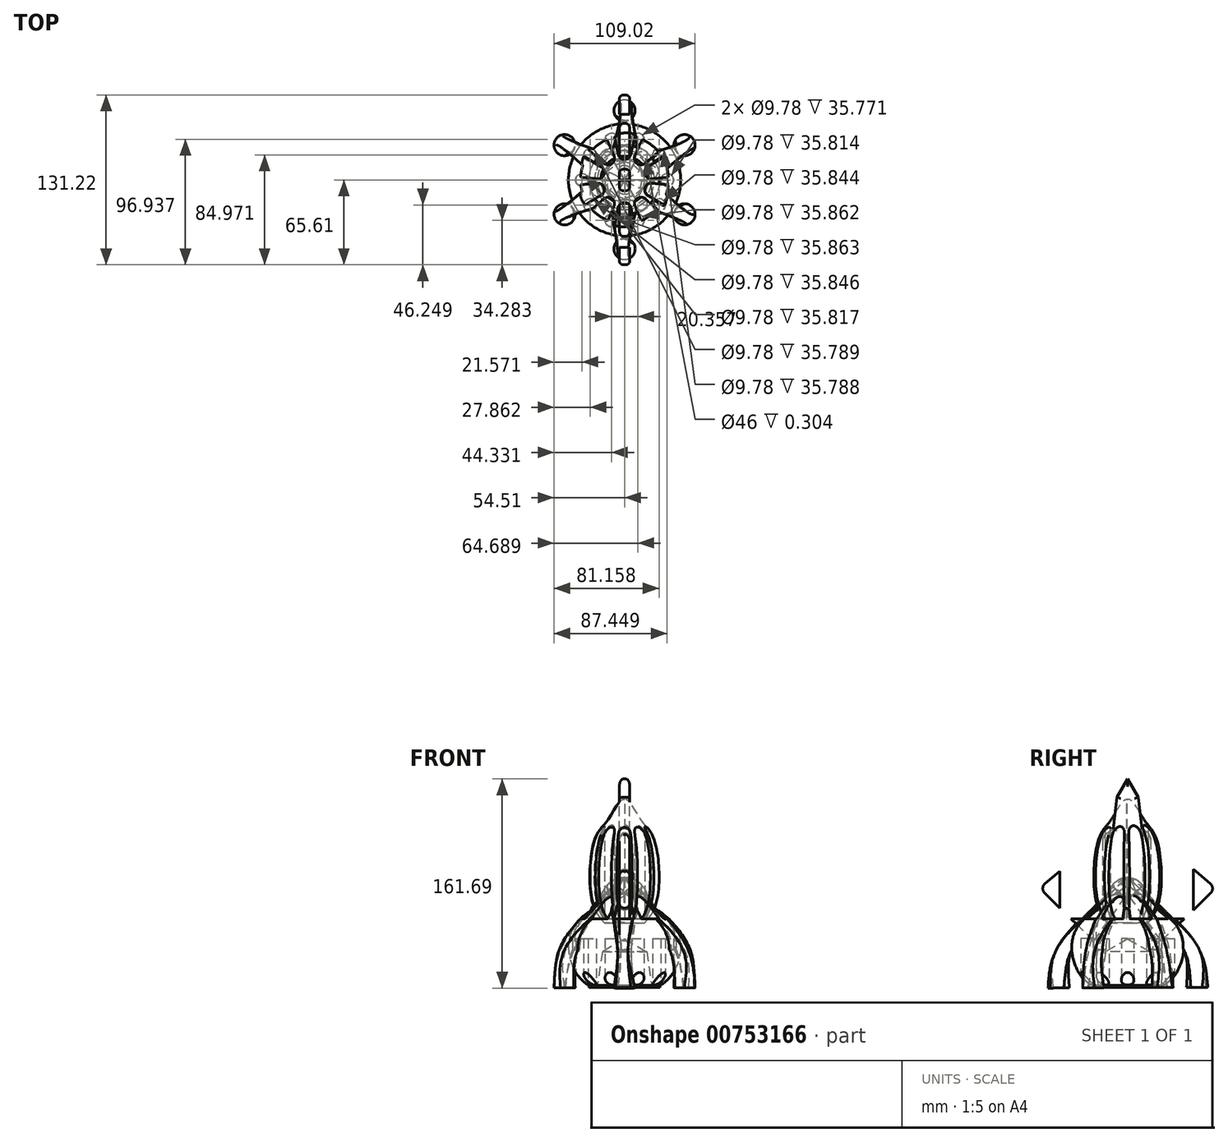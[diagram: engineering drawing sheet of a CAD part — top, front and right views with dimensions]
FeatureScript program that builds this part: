
annotation { "Feature Type Name" : "Feature", "Feature Type Description" : "" }
export const myFeature = defineFeature(function(context is Context, id is Id, definition is map)
    precondition{}
    {
        {
            var Q0;
            Q0=qCreatedBy(makeId("Top.planeOp"),FACE);
            cPlane(context, id + "F0", {"entities" : qUnion([Q0]), "cplaneType" : CPlaneType.OFFSET, "offset" : 28 * mm, "width" : 150 * mm, "height" : 150 * mm});
        }
        {
            var Q0;
            Q0=qCreatedBy(makeId("Top.planeOp"),FACE);
            var sketch = newSketch(context, id + "F1", { "sketchPlane" : qUnion([Q0])});
            skCircle(sketch, "E0", {"center": v(0, -53.65) * mm, "radius": 8.2 * mm});
            skCircle(sketch, "E1.1.0", {"center": v(46.46, -26.82) * mm, "radius": 8.2 * mm});
            skCircle(sketch, "E1.2.0", {"center": v(46.46, 26.82) * mm, "radius": 8.2 * mm});
            skCircle(sketch, "E1.4.0", {"center": v(-46.46, 26.82) * mm, "radius": 8.2 * mm});
            skPoint(sketch, "E1.center", {"position": v(0, 0) * mm});
            skCircle(sketch, "E2.1.5.0", {"center": v(-46.46, -26.82) * mm, "radius": 8.2 * mm});
            skArc(sketch, "E3", {"start": v(7.17, 57.63) * mm, "mid": v(1.7, 61.67) * mm, "end": v(-4.94, 60.2) * mm});
            skArc(sketch, "E4", {"start": v(6.58, 48.75) * mm, "mid": v(8.18, 53.1) * mm, "end": v(7.17, 57.63) * mm});
            skArc(sketch, "E5", {"start": v(-7.1, 49.56) * mm, "mid": v(-0.48, 45.47) * mm, "end": v(6.58, 48.75) * mm});
            skArc(sketch, "E6", {"start": v(-4.94, 60.2) * mm, "mid": v(-8.03, 55.29) * mm, "end": v(-7.1, 49.56) * mm});
            skSolve(sketch);
        }
        {
            var Q0;
            Q0=qCreatedBy(makeId("Right.planeOp"),FACE);
            var sketch = newSketch(context, id + "F2", { "sketchPlane" : qUnion([Q0])});
            skFitSpline(sketch, "E7", {"points": [v(53.84, 0) * mm, v(45.06, 43.34) * mm, v(0, 67.01) * mm], "startDerivative": vector(-1.6, 100.47) * mm, "endDerivative": vector(-104.87, 34.33) * mm});
            skSolve(sketch);
        }
        {
            var Q0;
            Q0=qCreatedBy(id+"F0.planeOp",FACE);
            var sketch = newSketch(context, id + "F3", { "sketchPlane" : qUnion([Q0])});
            skLineSegment(sketch, "E8.bottom", {"start": v(-2.65, 55.9) * mm, "end": v(5.35, 55.9) * mm});
            skLineSegment(sketch, "E8.top", {"start": v(-2.65, 43.9) * mm, "end": v(5.35, 43.9) * mm});
            skLineSegment(sketch, "E8.left", {"start": v(-2.65, 55.9) * mm, "end": v(-2.65, 43.9) * mm});
            skLineSegment(sketch, "E8.right", {"start": v(5.35, 55.9) * mm, "end": v(5.35, 43.9) * mm});
            skLineSegment(sketch, "E9.1.0", {"start": v(-55.65, 13.56) * mm, "end": v(-53.18, 21.17) * mm});
            skLineSegment(sketch, "E9.1.1", {"start": v(-44.24, 9.85) * mm, "end": v(-41.77, 17.46) * mm});
            skLineSegment(sketch, "E9.1.2", {"start": v(-55.65, 13.56) * mm, "end": v(-44.24, 9.85) * mm});
            skLineSegment(sketch, "E9.1.3", {"start": v(-53.18, 21.17) * mm, "end": v(-41.77, 17.46) * mm});
            skLineSegment(sketch, "E9.2.0", {"start": v(-31.77, -49.94) * mm, "end": v(-38.24, -45.23) * mm});
            skLineSegment(sketch, "E9.2.1", {"start": v(-24.71, -40.23) * mm, "end": v(-31.19, -35.53) * mm});
            skLineSegment(sketch, "E9.2.2", {"start": v(-31.77, -49.94) * mm, "end": v(-24.71, -40.23) * mm});
            skLineSegment(sketch, "E9.2.3", {"start": v(-38.24, -45.23) * mm, "end": v(-31.19, -35.53) * mm});
            skLineSegment(sketch, "E9.3.0", {"start": v(36, -46.84) * mm, "end": v(29.53, -51.54) * mm});
            skLineSegment(sketch, "E9.3.1", {"start": v(28.95, -37.13) * mm, "end": v(22.48, -41.83) * mm});
            skLineSegment(sketch, "E9.3.2", {"start": v(36, -46.84) * mm, "end": v(28.95, -37.13) * mm});
            skLineSegment(sketch, "E9.3.3", {"start": v(29.53, -51.54) * mm, "end": v(22.48, -41.83) * mm});
            skLineSegment(sketch, "E9.4.0", {"start": v(54, 18.57) * mm, "end": v(56.47, 10.96) * mm});
            skLineSegment(sketch, "E9.4.1", {"start": v(42.58, 14.86) * mm, "end": v(45.06, 7.25) * mm});
            skLineSegment(sketch, "E9.4.2", {"start": v(54, 18.57) * mm, "end": v(42.58, 14.86) * mm});
            skLineSegment(sketch, "E9.4.3", {"start": v(56.47, 10.96) * mm, "end": v(45.06, 7.25) * mm});
            skPoint(sketch, "E9.center", {"position": v(-0.02, -1.75) * mm});
            skSolve(sketch);
        }
        {
            var Q0;
            Q0=qCreatedBy(makeId("Right.planeOp"),FACE);
            var sketch = newSketch(context, id + "F4", { "sketchPlane" : qUnion([Q0])});
            skLineSegment(sketch, "E10", {"start": v(0.18, 0) * mm, "end": v(-21.05, 0) * mm});
            skFitSpline(sketch, "E11", {"points": [v(-21.05, 0) * mm, v(-42.02, 40.3) * mm, v(-8.37, 66.57) * mm, v(-0.13, 65.47) * mm], "startDerivative": vector(-109.76, 0) * mm, "endDerivative": vector(42.44, -18.45) * mm});
            skLineSegment(sketch, "E12", {"start": v(-0.13, 65.47) * mm, "end": v(0.18, 0) * mm});
            skLineSegment(sketch, "E13", {"start": v(-21.05, 0) * mm, "end": v(-17.07, 27.44) * mm});
            skLineSegment(sketch, "E14", {"start": v(-17.07, 27.44) * mm, "end": v(0, 37.41) * mm});
            skSolve(sketch);
        }
        {
            var Q0;
            {var subQ0=sQuery(id+"F4.wireOp",EDGE,"E11");Q0=makeQuery(id+"F4.imprint","IMPRINT",FACE,{"disambiguationData":[TD([[makeQuery(id+"F4.imprint","IMPRINT",EDGE,{"derivedFrom":subQ0}),-1.0]])]});}
            var Q1;
            Q1=sQuery(id+"F4.wireOp",EDGE,"E12");
            revolve(context, id + "F5", {"surfaceOperationType" : NewSurfaceOperationType.NEW, "entities" : qUnion([Q0]), "axis" : qUnion([Q1]), "revolveType" : RevolveType.FULL});
        }
        {
            var Q0;
            Q0=qCreatedBy(id+"F0.planeOp",FACE);
            cPlane(context, id + "F6", {"entities" : qUnion([Q0]), "cplaneType" : CPlaneType.OFFSET, "offset" : 25 * mm, "width" : 150 * mm, "height" : 150 * mm});
        }
        {
            var Q0;
            Q0=qCreatedBy(makeId("Front.planeOp"),FACE);
            var sketch = newSketch(context, id + "F7", { "sketchPlane" : qUnion([Q0])});
            skArc(sketch, "E15", {"start": v(-13.56, 78.8) * mm, "mid": v(-18.17, 66.48) * mm, "end": v(-13.26, 54.27) * mm});
            skArc(sketch, "E16", {"start": v(-13.26, 54.27) * mm, "mid": v(2.4, 48.69) * mm, "end": v(16.05, 58.17) * mm});
            skArc(sketch, "E17", {"start": v(16.05, 58.17) * mm, "mid": v(18.07, 68.66) * mm, "end": v(13.85, 78.48) * mm});
            skArc(sketch, "E18", {"start": v(13.85, 78.48) * mm, "mid": v(0.22, 84.88) * mm, "end": v(-13.56, 78.8) * mm});
            skSolve(sketch);
        }
        {
            var Q1;
            Q1=makeQuery(id+"F1.imprint","IMPRINT",FACE,{"disambiguationData":[TD([[makeQuery(id+"F1.imprint","IMPRINT",EDGE,{"derivedFrom":sQuery(id+"F1.wireOp",EDGE,"E3")}),1.0]])]});
            var Q2;
            Q2=makeQuery(id+"F3.imprint","IMPRINT",FACE,{"disambiguationData":[TD([[makeQuery(id+"F3.imprint","IMPRINT",EDGE,{"derivedFrom":sQuery(id+"F3.wireOp",EDGE,"E8.bottom")}),-1.0]])]});
            var Q3;
            Q3=makeQuery(id+"F7.imprint","IMPRINT",FACE,{"disambiguationData":[TD([[makeQuery(id+"F7.imprint","IMPRINT",EDGE,{"derivedFrom":sQuery(id+"F7.wireOp",EDGE,"E15")}),1.0]])]});
            var Q4;
            Q4=sQuery(id+"F2.wireOp",EDGE,"E7");
            loft(context, id + "F8", {"sheetProfilesArray" : [{ "sheetProfileEntities" : qUnion([Q1]) }, { "sheetProfileEntities" : qUnion([Q2]) }, { "sheetProfileEntities" : qUnion([Q3]) }], "guidesArray" : [{ "guideEntities" : qUnion([Q4]), "guideDerivativeType" : LoftGuideDerivativeType.DEFAULT, "guideDerivativeMagnitude" : 1 }]});
        }
        {
            var Q0;
            Q0=makeQuery(id+"F8.opLoft","SWEPT_BODY",BODY,{"disambiguationData":[OSD([makeQuery(id+"F1.imprint","IMPRINT",FACE,{"disambiguationData":[TD([[makeQuery(id+"F1.imprint","IMPRINT",EDGE,{"derivedFrom":sQuery(id+"F1.wireOp",EDGE,"E3")}),1.0]])]}),sQuery(id+"F3.wireOp",EDGE,"E8.left"),makeQuery(id+"F7.imprint","IMPRINT",FACE,{"disambiguationData":[TD([[makeQuery(id+"F7.imprint","IMPRINT",EDGE,{"derivedFrom":sQuery(id+"F7.wireOp",EDGE,"E15")}),1.0]])]})])]});
            var Q1;
            Q1=sQuery(id+"F4.wireOp",EDGE,"E12");
            circularPattern(context, id + "F9", {"operationType" : NewBodyOperationType.ADD, "entities" : qUnion([Q0]), "axis" : qUnion([Q1]), "angle" : 360 * degree, "instanceCount" : 6, "equalSpace" : true, "isCentered" : true});
        }
        {
            var Q0;
            Q0=qCreatedBy(makeId("Front.planeOp"),FACE);
            var sketch = newSketch(context, id + "F10", { "sketchPlane" : qUnion([Q0])});
            skFitSpline(sketch, "E19", {"points": [v(-15.35, 49.67) * mm, v(-24.47, 64.82) * mm, v(-25.38, 104.6) * mm, v(-19.75, 121) * mm, v(-12.6, 129.8) * mm, v(0, 145.27) * mm, v(10.93, 128.5) * mm], "startDerivative": vector(-59.94, 59.18) * mm, "endDerivative": vector(86, -27.64) * mm});
            skLineSegment(sketch, "E20", {"start": v(0, 50.04) * mm, "end": v(-15.35, 49.67) * mm});
            skLineSegment(sketch, "E21", {"start": v(0, 50.04) * mm, "end": v(0, 145.27) * mm});
            skSolve(sketch);
        }
        {
            var Q0;
            {var subQ0=sQuery(id+"F10.wireOp",EDGE,"E20");Q0=makeQuery(id+"F10.imprint","IMPRINT",FACE,{"disambiguationData":[TD([[makeQuery(id+"F10.imprint","IMPRINT",EDGE,{"derivedFrom":subQ0}),-1.0]])]});}
            var Q1;
            Q1=sQuery(id+"F10.wireOp",EDGE,"E21");
            revolve(context, id + "F11", {"surfaceOperationType" : NewSurfaceOperationType.NEW, "entities" : qUnion([Q0]), "axis" : qUnion([Q1]), "revolveType" : RevolveType.FULL});
        }
        {
            var Q0;
            {var subQ0=sQuery(id+"F10.wireOp",EDGE,"E20");Q0=makeQuery(id+"F10.imprint","IMPRINT",FACE,{"disambiguationData":[TD([[makeQuery(id+"F10.imprint","IMPRINT",EDGE,{"derivedFrom":subQ0}),-1.0]])]});}
            var Q1;
            Q1=sQuery(id+"F10.wireOp",EDGE,"E21");
            revolve(context, id + "F12", {"surfaceOperationType" : NewSurfaceOperationType.NEW, "entities" : qUnion([Q0]), "axis" : qUnion([Q1]), "revolveType" : RevolveType.FULL});
        }
        {
            var Q0;
            Q0=qCreatedBy(makeId("Right.planeOp"),FACE);
            var sketch = newSketch(context, id + "F13", { "sketchPlane" : qUnion([Q0])});
            skLineSegment(sketch, "E22", {"start": v(26.03, 35.86) * mm, "end": v(64.1, 72.83) * mm});
            skLineSegment(sketch, "E23", {"start": v(63.8, 80.26) * mm, "end": v(22.57, 114.6) * mm});
            skLineSegment(sketch, "E24", {"start": v(22.57, 114.6) * mm, "end": v(11.06, 122.62) * mm});
            skLineSegment(sketch, "E25", {"start": v(11.06, 122.62) * mm, "end": v(8.34, 146.93) * mm});
            skLineSegment(sketch, "E26", {"start": v(8.34, 146.93) * mm, "end": v(0, 161.11) * mm});
            skLineSegment(sketch, "E27", {"start": v(0, 161.11) * mm, "end": v(0, 10.58) * mm});
            skLineSegment(sketch, "E28.MirrorCS", {"start": v(-8.34, 146.93) * mm, "end": v(0, 161.11) * mm});
            skLineSegment(sketch, "E29.MirrorCS", {"start": v(-11.06, 122.62) * mm, "end": v(-8.34, 146.93) * mm});
            skLineSegment(sketch, "E30.MirrorCS", {"start": v(-63.8, 80.26) * mm, "end": v(-22.57, 114.6) * mm});
            skLineSegment(sketch, "E31.MirrorCS", {"start": v(-26.03, 35.86) * mm, "end": v(-64.1, 72.83) * mm});
            skLineSegment(sketch, "E32.MirrorCS", {"start": v(-22.57, 114.6) * mm, "end": v(-11.06, 122.62) * mm});
            skPoint(sketch, "E33", {"position": v(47.66, 93.7) * mm});
            skPoint(sketch, "E34.visualSharp", {"position": v(68.08, 76.7) * mm});
            skArc(sketch, "E34.filletArc", {"start": v(64.1, 72.83) * mm, "mid": v(65.6, 76.6) * mm, "end": v(63.8, 80.26) * mm});
            skPoint(sketch, "E35.visualSharp", {"position": v(-68.08, 76.7) * mm});
            skArc(sketch, "E35.filletArc", {"start": v(-63.8, 80.26) * mm, "mid": v(-65.6, 76.6) * mm, "end": v(-64.1, 72.83) * mm});
            skLineSegment(sketch, "E36", {"start": v(26.03, 35.86) * mm, "end": v(0, 72.2) * mm});
            skLineSegment(sketch, "E37.MirrorCS", {"start": v(-26.03, 35.86) * mm, "end": v(0, 72.2) * mm});
            skPoint(sketch, "E38.orphan", {"position": v(0, 10.58) * mm});
            skSolve(sketch);
        }
        {
            var Q0;
            Q0=qSketchRegion(id+"F13",true);
            extrude(context, id + "F14", {"entities" : qUnion([Q0]), "endBound" : BoundingType.SYMMETRIC, "depth" : 8 * mm, "offsetDistance" : 25 * mm});
        }
        {
            var Q0;
            Q0=makeQuery(id+"F14.opExtrude","CAP_FACE",FACE,{"disambiguationData":[OSD([sQuery(id+"F13.wireOp",EDGE,"E22"),sQuery(id+"F13.wireOp",EDGE,"E23"),sQuery(id+"F13.wireOp",EDGE,"E24"),sQuery(id+"F13.wireOp",EDGE,"E25"),sQuery(id+"F13.wireOp",EDGE,"E26"),sQuery(id+"F13.wireOp",EDGE,"E28.MirrorCS"),sQuery(id+"F13.wireOp",EDGE,"E29.MirrorCS"),sQuery(id+"F13.wireOp",EDGE,"E30.MirrorCS"),sQuery(id+"F13.wireOp",EDGE,"E31.MirrorCS"),sQuery(id+"F13.wireOp",EDGE,"E32.MirrorCS")])],"isStart":true});
            var Q1;
            Q1=makeQuery(id+"F14.opExtrude","CAP_FACE",FACE,{"disambiguationData":[OSD([sQuery(id+"F13.wireOp",EDGE,"E22"),sQuery(id+"F13.wireOp",EDGE,"E23"),sQuery(id+"F13.wireOp",EDGE,"E24"),sQuery(id+"F13.wireOp",EDGE,"E25"),sQuery(id+"F13.wireOp",EDGE,"E26"),sQuery(id+"F13.wireOp",EDGE,"E28.MirrorCS"),sQuery(id+"F13.wireOp",EDGE,"E29.MirrorCS"),sQuery(id+"F13.wireOp",EDGE,"E30.MirrorCS"),sQuery(id+"F13.wireOp",EDGE,"E31.MirrorCS"),sQuery(id+"F13.wireOp",EDGE,"E32.MirrorCS")])],"isStart":false});
            fillet(context, id + "F15", {"entities" : qUnion([Q0, Q1]), "radius" : 3 * mm, "tangentPropagation" : true, "allowEdgeOverflow" : false});
        }
        {
            var Q0;
            Q0=qCreatedBy(makeId("Top.planeOp"),FACE);
            var sketch = newSketch(context, id + "F16", { "sketchPlane" : qUnion([Q0])});
            skCircle(sketch, "E39", {"center": v(32.94, 0) * mm, "radius": 4.89 * mm});
            skCircle(sketch, "E40.1.0", {"center": v(26.65, 19.36) * mm, "radius": 4.89 * mm});
            skCircle(sketch, "E40.2.0", {"center": v(10.18, 31.33) * mm, "radius": 4.89 * mm});
            skCircle(sketch, "E40.3.0", {"center": v(-10.18, 31.33) * mm, "radius": 4.89 * mm});
            skCircle(sketch, "E40.4.0", {"center": v(-26.65, 19.36) * mm, "radius": 4.89 * mm});
            skPoint(sketch, "E40.center", {"position": v(0, 0) * mm});
            skCircle(sketch, "E41.1.5.0", {"center": v(-32.94, 0) * mm, "radius": 4.89 * mm});
            skCircle(sketch, "E41.1.6.0", {"center": v(-26.65, -19.36) * mm, "radius": 4.89 * mm});
            skCircle(sketch, "E41.1.7.0", {"center": v(-10.18, -31.33) * mm, "radius": 4.89 * mm});
            skCircle(sketch, "E41.1.8.0", {"center": v(10.18, -31.33) * mm, "radius": 4.89 * mm});
            skCircle(sketch, "E41.1.9.0", {"center": v(26.65, -19.36) * mm, "radius": 4.89 * mm});
            skSolve(sketch);
        }
        {
            var Q0;
            Q0=qSketchRegion(id+"F16",true);
            extrude(context, id + "F17", {"entities" : qUnion([Q0]), "operationType" : NewBodyOperationType.REMOVE, "depth" : 37.6 * mm, "offsetDistance" : 25 * mm});
        }
        {
            var Q0;
            Q0=qCreatedBy(id+"F6.planeOp",FACE);
            var sketch = newSketch(context, id + "F18", { "sketchPlane" : qUnion([Q0])});
            skLineSegment(sketch, "E42", {"start": v(4.87, -21.36) * mm, "end": v(11.93, -52.3) * mm});
            skLineSegment(sketch, "E43", {"start": v(11.93, -52.3) * mm, "end": v(0, -52.3) * mm});
            skLineSegment(sketch, "E44", {"start": v(0, -52.3) * mm, "end": v(0, 0) * mm});
            skLineSegment(sketch, "E45.MirrorCS", {"start": v(-4.87, -21.36) * mm, "end": v(-11.93, -52.3) * mm});
            skLineSegment(sketch, "E46.MirrorCS", {"start": v(-11.93, -52.3) * mm, "end": v(0, -52.3) * mm});
            skPoint(sketch, "E47.visualSharp", {"position": v(0, 0) * mm});
            skArc(sketch, "E47.filletArc", {"start": v(4.87, -21.36) * mm, "mid": v(0, -17.47) * mm, "end": v(-4.87, -21.36) * mm});
            skLineSegment(sketch, "E48.1.0", {"start": v(39.9, -35.44) * mm, "end": v(30.25, -42.46) * mm});
            skPoint(sketch, "E48.1.1", {"position": v(-0.48, -0.15) * mm});
            skLineSegment(sketch, "E48.1.2", {"start": v(16.01, -14.57) * mm, "end": v(39.9, -35.44) * mm});
            skArc(sketch, "E48.1.3", {"start": v(16.01, -14.57) * mm, "mid": v(9.79, -14.29) * mm, "end": v(8.13, -20.3) * mm});
            skLineSegment(sketch, "E48.1.4", {"start": v(8.13, -20.3) * mm, "end": v(20.6, -49.47) * mm});
            skLineSegment(sketch, "E48.1.5", {"start": v(20.6, -49.47) * mm, "end": v(30.25, -42.46) * mm});
            skLineSegment(sketch, "E48.1.6", {"start": v(30.25, -42.46) * mm, "end": v(-0.48, -0.15) * mm});
            skLineSegment(sketch, "E48.2.0", {"start": v(52.63, -5.37) * mm, "end": v(48.95, -16.72) * mm});
            skPoint(sketch, "E48.2.1", {"position": v(-0.79, -0.56) * mm});
            skLineSegment(sketch, "E48.2.2", {"start": v(21.03, -2.52) * mm, "end": v(52.63, -5.37) * mm});
            skArc(sketch, "E48.2.3", {"start": v(21.03, -2.52) * mm, "mid": v(15.83, -5.96) * mm, "end": v(18.02, -11.8) * mm});
            skLineSegment(sketch, "E48.2.4", {"start": v(18.02, -11.8) * mm, "end": v(45.26, -28.07) * mm});
            skLineSegment(sketch, "E48.2.5", {"start": v(45.26, -28.07) * mm, "end": v(48.95, -16.72) * mm});
            skLineSegment(sketch, "E48.2.6", {"start": v(48.95, -16.72) * mm, "end": v(-0.79, -0.56) * mm});
            skLineSegment(sketch, "E48.3.0", {"start": v(45.25, 26.44) * mm, "end": v(48.94, 15.1) * mm});
            skPoint(sketch, "E48.3.1", {"position": v(-0.8, -1.07) * mm});
            skLineSegment(sketch, "E48.3.2", {"start": v(18.02, 10.17) * mm, "end": v(45.25, 26.44) * mm});
            skArc(sketch, "E48.3.3", {"start": v(18.02, 10.17) * mm, "mid": v(15.83, 4.33) * mm, "end": v(21.03, 0.9) * mm});
            skLineSegment(sketch, "E48.3.4", {"start": v(21.03, 0.9) * mm, "end": v(52.63, 3.74) * mm});
            skLineSegment(sketch, "E48.3.5", {"start": v(52.63, 3.74) * mm, "end": v(48.94, 15.1) * mm});
            skLineSegment(sketch, "E48.3.6", {"start": v(48.94, 15.1) * mm, "end": v(-0.8, -1.07) * mm});
            skLineSegment(sketch, "E48.4.0", {"start": v(20.59, 47.84) * mm, "end": v(30.24, 40.82) * mm});
            skPoint(sketch, "E48.4.1", {"position": v(-0.5, -1.48) * mm});
            skLineSegment(sketch, "E48.4.2", {"start": v(8.12, 18.66) * mm, "end": v(20.59, 47.84) * mm});
            skArc(sketch, "E48.4.3", {"start": v(8.12, 18.66) * mm, "mid": v(9.77, 12.65) * mm, "end": v(16, 12.93) * mm});
            skLineSegment(sketch, "E48.4.4", {"start": v(16, 12.93) * mm, "end": v(39.9, 33.8) * mm});
            skLineSegment(sketch, "E48.4.5", {"start": v(39.9, 33.8) * mm, "end": v(30.24, 40.82) * mm});
            skLineSegment(sketch, "E48.4.6", {"start": v(30.24, 40.82) * mm, "end": v(-0.5, -1.48) * mm});
            skLineSegment(sketch, "E48.5.0", {"start": v(-11.95, 50.65) * mm, "end": v(-0.01, 50.65) * mm});
            skPoint(sketch, "E48.5.1", {"position": v(-0.01, -1.64) * mm});
            skLineSegment(sketch, "E48.5.2", {"start": v(-4.89, 19.72) * mm, "end": v(-11.95, 50.65) * mm});
            skArc(sketch, "E48.5.3", {"start": v(-4.89, 19.72) * mm, "mid": v(-0.01, 15.83) * mm, "end": v(4.86, 19.72) * mm});
            skLineSegment(sketch, "E48.5.4", {"start": v(4.86, 19.72) * mm, "end": v(11.92, 50.65) * mm});
            skLineSegment(sketch, "E48.5.5", {"start": v(11.92, 50.65) * mm, "end": v(-0.01, 50.65) * mm});
            skLineSegment(sketch, "E48.5.6", {"start": v(-0.01, 50.65) * mm, "end": v(-0.01, -1.64) * mm});
            skLineSegment(sketch, "E48.6.0", {"start": v(-39.92, 33.8) * mm, "end": v(-30.27, 40.82) * mm});
            skPoint(sketch, "E48.6.1", {"position": v(0.47, -1.49) * mm});
            skLineSegment(sketch, "E48.6.2", {"start": v(-16.03, 12.93) * mm, "end": v(-39.92, 33.8) * mm});
            skArc(sketch, "E48.6.3", {"start": v(-16.03, 12.93) * mm, "mid": v(-9.8, 12.65) * mm, "end": v(-8.14, 18.66) * mm});
            skLineSegment(sketch, "E48.6.4", {"start": v(-8.14, 18.66) * mm, "end": v(-20.61, 47.83) * mm});
            skLineSegment(sketch, "E48.6.5", {"start": v(-20.61, 47.83) * mm, "end": v(-30.27, 40.82) * mm});
            skLineSegment(sketch, "E48.6.6", {"start": v(-30.27, 40.82) * mm, "end": v(0.47, -1.49) * mm});
            skLineSegment(sketch, "E48.7.0", {"start": v(-52.65, 3.73) * mm, "end": v(-48.96, 15.08) * mm});
            skPoint(sketch, "E48.7.1", {"position": v(0.77, -1.08) * mm});
            skLineSegment(sketch, "E48.7.2", {"start": v(-21.05, 0.88) * mm, "end": v(-52.65, 3.73) * mm});
            skArc(sketch, "E48.7.3", {"start": v(-21.05, 0.88) * mm, "mid": v(-15.85, 4.32) * mm, "end": v(-18.04, 10.16) * mm});
            skLineSegment(sketch, "E48.7.4", {"start": v(-18.04, 10.16) * mm, "end": v(-45.27, 26.43) * mm});
            skLineSegment(sketch, "E48.7.5", {"start": v(-45.27, 26.43) * mm, "end": v(-48.96, 15.08) * mm});
            skLineSegment(sketch, "E48.7.6", {"start": v(-48.96, 15.08) * mm, "end": v(0.77, -1.08) * mm});
            skLineSegment(sketch, "E48.8.0", {"start": v(-45.27, -28.08) * mm, "end": v(-48.96, -16.73) * mm});
            skPoint(sketch, "E48.8.1", {"position": v(0.78, -0.57) * mm});
            skLineSegment(sketch, "E48.8.2", {"start": v(-18.03, -11.81) * mm, "end": v(-45.27, -28.08) * mm});
            skArc(sketch, "E48.8.3", {"start": v(-18.03, -11.81) * mm, "mid": v(-15.84, -5.97) * mm, "end": v(-21.04, -2.54) * mm});
            skLineSegment(sketch, "E48.8.4", {"start": v(-21.04, -2.54) * mm, "end": v(-52.64, -5.38) * mm});
            skLineSegment(sketch, "E48.8.5", {"start": v(-52.64, -5.38) * mm, "end": v(-48.96, -16.73) * mm});
            skLineSegment(sketch, "E48.8.6", {"start": v(-48.96, -16.73) * mm, "end": v(0.78, -0.57) * mm});
            skLineSegment(sketch, "E48.9.0", {"start": v(-20.6, -49.48) * mm, "end": v(-30.25, -42.46) * mm});
            skPoint(sketch, "E48.9.1", {"position": v(0.48, -0.16) * mm});
            skLineSegment(sketch, "E48.9.2", {"start": v(-8.13, -20.3) * mm, "end": v(-20.6, -49.48) * mm});
            skArc(sketch, "E48.9.3", {"start": v(-8.13, -20.3) * mm, "mid": v(-9.79, -14.3) * mm, "end": v(-16.02, -14.58) * mm});
            skLineSegment(sketch, "E48.9.4", {"start": v(-16.02, -14.58) * mm, "end": v(-39.9, -35.45) * mm});
            skLineSegment(sketch, "E48.9.5", {"start": v(-39.9, -35.45) * mm, "end": v(-30.25, -42.46) * mm});
            skLineSegment(sketch, "E48.9.6", {"start": v(-30.25, -42.46) * mm, "end": v(0.48, -0.16) * mm});
            skPoint(sketch, "E48.center", {"position": v(0, -0.82) * mm});
            skSolve(sketch);
        }
        {
            var Q0;
            Q0=qSketchRegion(id+"F18",true);
            extrude(context, id + "F19", {"entities" : qUnion([Q0]), "operationType" : NewBodyOperationType.REMOVE, "depth" : 88.7 * mm, "offsetDistance" : 25 * mm});
        }
        {
            var Q0;
            Q0=makeQuery(id+"F19.boolean.opBoolean","COPY",FACE,{"derivedFrom":makeQuery(id+"F19.opExtrude","SWEPT_FACE",FACE,{"disambiguationData":[OSD([sQuery(id+"F18.wireOp",EDGE,"E48.2.3")])]})});
            var Q1;
            Q1=makeQuery(id+"F19.boolean.opBoolean","COPY",FACE,{"derivedFrom":makeQuery(id+"F19.opExtrude","SWEPT_FACE",FACE,{"disambiguationData":[OSD([sQuery(id+"F18.wireOp",EDGE,"E48.3.3")])]})});
            var Q2;
            Q2=makeQuery(id+"F19.boolean.opBoolean","COPY",FACE,{"derivedFrom":makeQuery(id+"F19.opExtrude","SWEPT_FACE",FACE,{"disambiguationData":[OSD([sQuery(id+"F18.wireOp",EDGE,"E48.4.3")])]})});
            fillet(context, id + "F20", {"entities" : qUnion([Q0, Q1, Q2]), "radius" : 1 * mm, "tangentPropagation" : true, "allowEdgeOverflow" : false});
        }
        {
            var Q0;
            Q0=qCreatedBy(makeId("Top.planeOp"),FACE);
            var sketch = newSketch(context, id + "F21", { "sketchPlane" : qUnion([Q0])});
            skCircle(sketch, "E49", {"center": v(0, 0) * mm, "radius": 23 * mm});
            skCircle(sketch, "E50", {"center": v(0, 0) * mm, "radius": 27.37 * mm});
            skSolve(sketch);
        }
        {
            var Q0;
            Q0=qSketchRegion(id+"F21",true);
            extrude(context, id + "F22", {"entities" : qUnion([Q0]), "operationType" : NewBodyOperationType.ADD, "depth" : 3 * mm, "offsetDistance" : 25 * mm});
        }
    });
